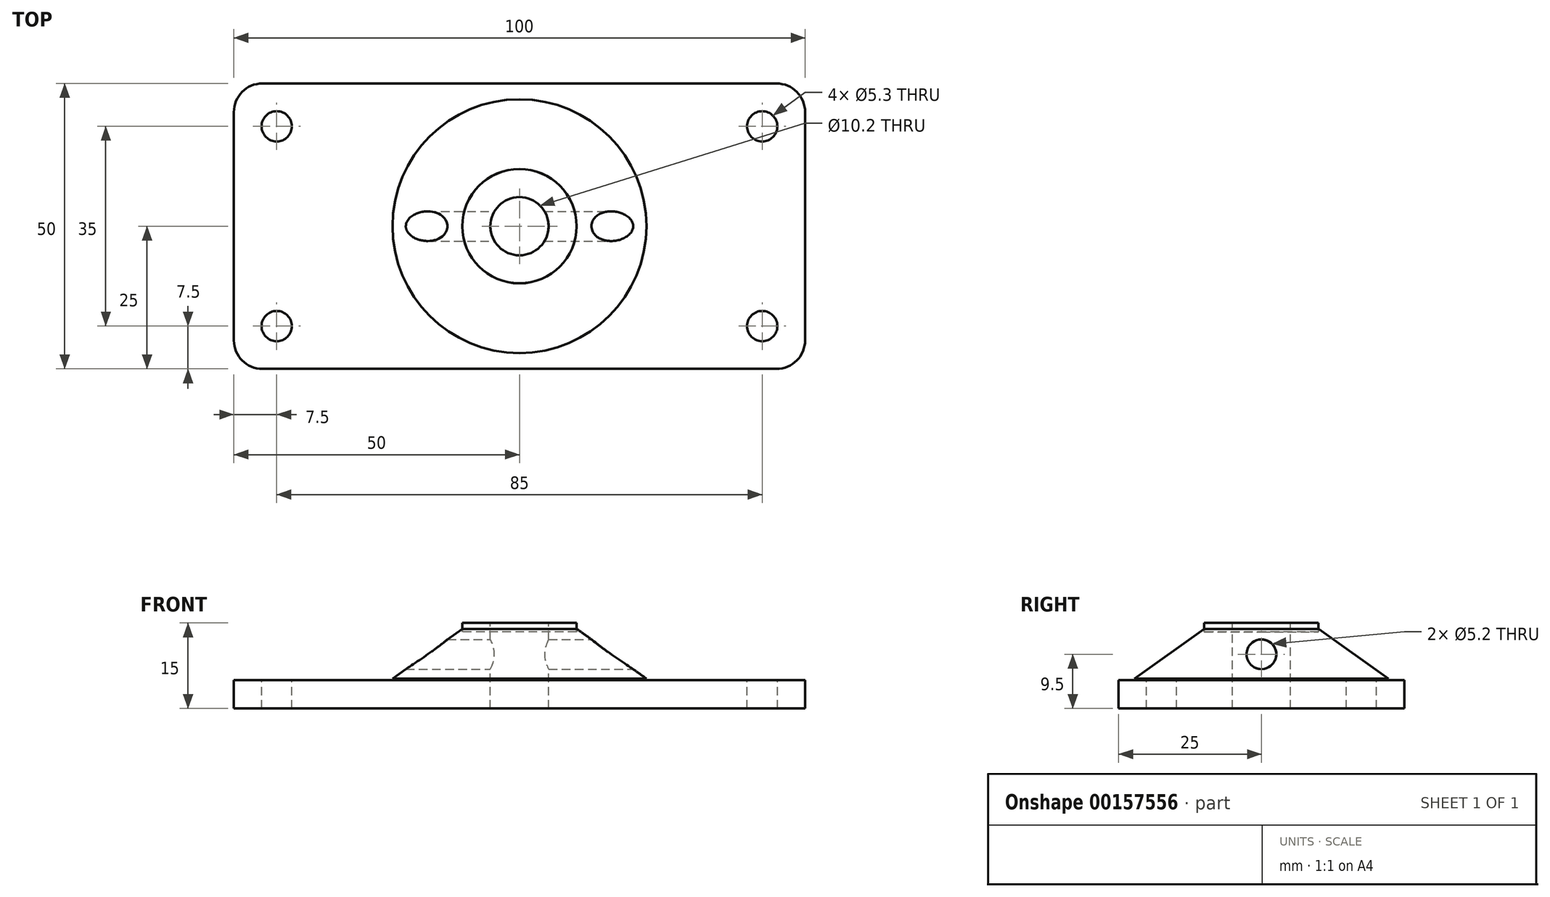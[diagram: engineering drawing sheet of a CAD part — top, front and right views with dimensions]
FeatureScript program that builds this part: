
annotation { "Feature Type Name" : "Feature", "Feature Type Description" : "" }
export const myFeature = defineFeature(function(context is Context, id is Id, definition is map)
    precondition{}
    {
        {
            var Q0;
            Q0=qCreatedBy(makeId("Top.planeOp"),FACE);
            var sketch = newSketch(context, id + "F0", { "sketchPlane" : qUnion([Q0])});
            skLineSegment(sketch, "E0.bottom", {"start": v(50, 25) * mm, "end": v(-50, 25) * mm});
            skLineSegment(sketch, "E0.top", {"start": v(50, -25) * mm, "end": v(-50, -25) * mm});
            skLineSegment(sketch, "E0.left", {"start": v(50, 25) * mm, "end": v(50, -25) * mm});
            skLineSegment(sketch, "E0.right", {"start": v(-50, 25) * mm, "end": v(-50, -25) * mm});
            skPoint(sketch, "E0.middle", {"position": v(0, 0) * mm});
            skSolve(sketch);
        }
        {
            var Q0;
            Q0=makeQuery(id+"F0.imprint","IMPRINT",FACE,{"disambiguationData":[TD([[makeQuery(id+"F0.imprint","IMPRINT",EDGE,{"derivedFrom":sQuery(id+"F0.wireOp",EDGE,"E0.bottom")}),1.0]])]});
            extrude(context, id + "F1", {"entities" : qUnion([Q0]), "depth" : 5 * mm});
        }
        {
            var Q0;
            Q0=makeQuery(id+"F1.opExtrude","CAP_FACE",FACE,{"disambiguationData":[OSD([sQuery(id+"F0.wireOp",EDGE,"E0.bottom"),sQuery(id+"F0.wireOp",EDGE,"E0.top"),sQuery(id+"F0.wireOp",EDGE,"E0.left"),sQuery(id+"F0.wireOp",EDGE,"E0.right")])],"isStart":false});
            var sketch = newSketch(context, id + "F2", { "sketchPlane" : qUnion([Q0])});
            skCircle(sketch, "E1", {"center": v(0, 0) * mm, "radius": 10 * mm});
            skSolve(sketch);
        }
        {
            var Q0;
            Q0=makeQuery(id+"F2.imprint","IMPRINT",FACE,{"disambiguationData":[TD([[makeQuery(id+"F2.imprint","IMPRINT",EDGE,{"derivedFrom":sQuery(id+"F2.wireOp",EDGE,"E1")}),1.0]])]});
            extrude(context, id + "F3", {"entities" : qUnion([Q0]), "operationType" : NewBodyOperationType.ADD, "depth" : 10 * mm});
        }
        {
            var Q0;
            Q0=makeQuery(id+"F3.opExtrude","CAP_FACE",FACE,{"disambiguationData":[OSD([sQuery(id+"F2.wireOp",EDGE,"E1")])],"isStart":false});
            var sketch = newSketch(context, id + "F4", { "sketchPlane" : qUnion([Q0])});
            skCircle(sketch, "E2", {"center": v(0, 0) * mm, "radius": 5.1 * mm});
            skSolve(sketch);
        }
        {
            var Q0;
            Q0=makeQuery(id+"F4.imprint","IMPRINT",FACE,{"disambiguationData":[TD([[makeQuery(id+"F4.imprint","IMPRINT",EDGE,{"derivedFrom":sQuery(id+"F4.wireOp",EDGE,"E2")}),1.0]])]});
            extrude(context, id + "F5", {"entities" : qUnion([Q0]), "operationType" : NewBodyOperationType.REMOVE, "oppositeDirection" : true, "depth" : 25 * mm});
        }
        {
            var Q0;
            Q0=makeQuery(id+"F1.opExtrude","SWEPT_EDGE",EDGE,{"disambiguationData":[OSD([sQuery(id+"F0.wireOp",EDGE,"E0.top"),sQuery(id+"F0.wireOp",EDGE,"E0.right")])]});
            var Q1;
            Q1=makeQuery(id+"F1.opExtrude","SWEPT_EDGE",EDGE,{"disambiguationData":[OSD([sQuery(id+"F0.wireOp",EDGE,"E0.bottom"),sQuery(id+"F0.wireOp",EDGE,"E0.right")])]});
            var Q2;
            Q2=makeQuery(id+"F1.opExtrude","SWEPT_EDGE",EDGE,{"disambiguationData":[OSD([sQuery(id+"F0.wireOp",EDGE,"E0.bottom"),sQuery(id+"F0.wireOp",EDGE,"E0.left")])]});
            var Q3;
            Q3=makeQuery(id+"F1.opExtrude","SWEPT_EDGE",EDGE,{"disambiguationData":[OSD([sQuery(id+"F0.wireOp",EDGE,"E0.top"),sQuery(id+"F0.wireOp",EDGE,"E0.left")])]});
            fillet(context, id + "F6", {"entities" : qUnion([Q0, Q1, Q2, Q3]), "radius" : 5 * mm, "tangentPropagation" : true, "allowEdgeOverflow" : false});
        }
        {
            var Q0;
            Q0=makeQuery(id+"F1.opExtrude","CAP_FACE",FACE,{"disambiguationData":[OSD([sQuery(id+"F0.wireOp",EDGE,"E0.bottom"),sQuery(id+"F0.wireOp",EDGE,"E0.top"),sQuery(id+"F0.wireOp",EDGE,"E0.left"),sQuery(id+"F0.wireOp",EDGE,"E0.right")])],"isStart":false});
            var sketch = newSketch(context, id + "F7", { "sketchPlane" : qUnion([Q0])});
            skPoint(sketch, "E3.middle", {"position": v(0, 0) * mm});
            skLineSegment(sketch, "E4.bottom", {"start": v(-42.5, -17.5) * mm, "end": v(42.5, -17.5) * mm, "construction": true});
            skLineSegment(sketch, "E4.top", {"start": v(-42.5, 17.5) * mm, "end": v(42.5, 17.5) * mm, "construction": true});
            skLineSegment(sketch, "E4.left", {"start": v(-42.5, -17.5) * mm, "end": v(-42.5, 17.5) * mm, "construction": true});
            skLineSegment(sketch, "E4.right", {"start": v(42.5, -17.5) * mm, "end": v(42.5, 17.5) * mm, "construction": true});
            skCircle(sketch, "E5", {"center": v(-42.5, -17.5) * mm, "radius": 2.65 * mm});
            skCircle(sketch, "E6", {"center": v(-42.5, 17.5) * mm, "radius": 2.65 * mm});
            skCircle(sketch, "E7", {"center": v(42.5, 17.5) * mm, "radius": 2.65 * mm});
            skCircle(sketch, "E8", {"center": v(42.5, -17.5) * mm, "radius": 2.65 * mm});
            skSolve(sketch);
        }
        {
            var Q0;
            Q0=makeQuery(id+"F7.imprint","IMPRINT",FACE,{"disambiguationData":[TD([[makeQuery(id+"F7.imprint","IMPRINT",EDGE,{"derivedFrom":sQuery(id+"F7.wireOp",EDGE,"E7")}),1.0]])]});
            var Q1;
            Q1=makeQuery(id+"F7.imprint","IMPRINT",FACE,{"disambiguationData":[TD([[makeQuery(id+"F7.imprint","IMPRINT",EDGE,{"derivedFrom":sQuery(id+"F7.wireOp",EDGE,"E8")}),1.0]])]});
            var Q2;
            Q2=makeQuery(id+"F7.imprint","IMPRINT",FACE,{"disambiguationData":[TD([[makeQuery(id+"F7.imprint","IMPRINT",EDGE,{"derivedFrom":sQuery(id+"F7.wireOp",EDGE,"E5")}),1.0]])]});
            var Q3;
            Q3=makeQuery(id+"F7.imprint","IMPRINT",FACE,{"disambiguationData":[TD([[makeQuery(id+"F7.imprint","IMPRINT",EDGE,{"derivedFrom":sQuery(id+"F7.wireOp",EDGE,"E6")}),1.0]])]});
            extrude(context, id + "F8", {"entities" : qUnion([Q0, Q1, Q2, Q3]), "operationType" : NewBodyOperationType.REMOVE, "oppositeDirection" : true, "depth" : 25 * mm});
        }
        {
            var Q0;
            Q0=qCreatedBy(makeId("Front.planeOp"),FACE);
            var sketch = newSketch(context, id + "F9", { "sketchPlane" : qUnion([Q0])});
            skLineSegment(sketch, "E9", {"start": v(10.01, 13.96) * mm, "end": v(22.23, 5.24) * mm});
            skLineSegment(sketch, "E10", {"start": v(22.23, 5.24) * mm, "end": v(9.8, 5.24) * mm});
            skLineSegment(sketch, "E11", {"start": v(9.8, 5.24) * mm, "end": v(10.01, 13.96) * mm});
            skSolve(sketch);
        }
        {
            var Q0;
            Q0=makeQuery(id+"F9.imprint","IMPRINT",FACE,{"disambiguationData":[TD([[makeQuery(id+"F9.imprint","IMPRINT",EDGE,{"derivedFrom":sQuery(id+"F9.wireOp",EDGE,"E9")}),-1.0]])]});
            var Q1;
            Q1=makeQuery(id+"F3.opExtrude","SWEPT_FACE",FACE,{"disambiguationData":[OSD([sQuery(id+"F2.wireOp",EDGE,"E1")])]});
            revolve(context, id + "F10", {"operationType" : NewBodyOperationType.ADD, "entities" : qUnion([Q0]), "axis" : qUnion([Q1]), "revolveType" : RevolveType.FULL});
        }
        {
            var Q0;
            Q0=qCreatedBy(makeId("Right.planeOp"),FACE);
            var sketch = newSketch(context, id + "F11", { "sketchPlane" : qUnion([Q0])});
            skCircle(sketch, "E12", {"center": v(0, 9.5) * mm, "radius": 2.6 * mm});
            skSolve(sketch);
        }
        {
            var Q0;
            Q0=makeQuery(id+"F11.imprint","IMPRINT",FACE,{"disambiguationData":[TD([[makeQuery(id+"F11.imprint","IMPRINT",EDGE,{"derivedFrom":sQuery(id+"F11.wireOp",EDGE,"E12")}),1.0]])]});
            extrude(context, id + "F12", {"entities" : qUnion([Q0]), "operationType" : NewBodyOperationType.REMOVE, "oppositeDirection" : true, "depth" : 25 * mm, "hasSecondDirection" : true, "secondDirectionOppositeDirection" : false, "secondDirectionDepth" : 25 * mm});
        }
    });
